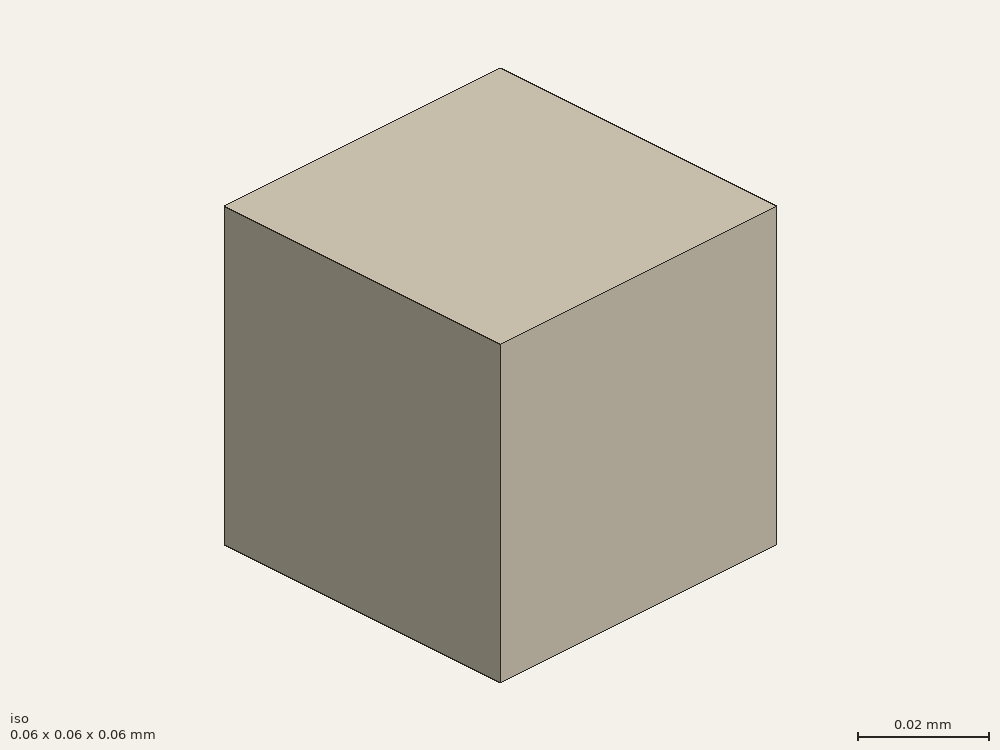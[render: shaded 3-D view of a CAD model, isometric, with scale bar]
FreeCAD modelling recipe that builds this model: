
FCSTD DOCUMENT  (FreeCAD 0.21R33694 (Git))
Label: dipole
License: All rights reserved
LicenseURL: http://en.wikipedia.org/wiki/All_rights_reserved
objects: Part::Part2DObjectPython×22, Part::Extrusion×13, Part::Cut×11, App::FeaturePython×9, Part::FeaturePython×8
note: 54 computed .brp shape members not serialized (recipe doc carries the construction recipe); baked Part::Feature solids carry a one-line shape summary decoded from their .brp

FEATURE [Part::Part2DObjectPython] Polygon  # Draft 2D object (typed FeaturePython)
  Area = 0.0027
  ChamferSize = 0
  DrawMode = 0
  FacesNumber = 12
  FilletRadius = 0
  MakeFace = true
  Placement = pos=(0,0,0.05) rot=(0,0,1;0rad)
  Radius = 0.03
FEATURE [Part::Extrusion] Extrude  label="antenna1"
  Base = -> Polygon
  Dir = (0,0,1)
  DirMode = 2
  FaceMakerClass = Part::FaceMakerBullseye
  LengthFwd = 7.45
  LengthRev = 0
  Solid = false
  Symmetric = false
FEATURE [Part::Part2DObjectPython] Polygon002  # Draft 2D object (typed FeaturePython)
  Area = 0.12
  ChamferSize = 0
  DrawMode = 0
  FacesNumber = 12
  FilletRadius = 0
  MakeFace = true
  Radius = 0.2
FEATURE [Part::Part2DObjectPython] Polygon003  # Draft 2D object (typed FeaturePython)
  Area = 0.48
  ChamferSize = 0
  DrawMode = 0
  FacesNumber = 12
  FilletRadius = 0
  MakeFace = true
  Radius = 0.4
FEATURE [Part::Part2DObjectPython] Polygon004  # Draft 2D object (typed FeaturePython)
  Area = 27
  ChamferSize = 0
  DrawMode = 0
  FacesNumber = 12
  FilletRadius = 0
  MakeFace = true
  Radius = 3
FEATURE [Part::Part2DObjectPython] Polygon005  # Draft 2D object (typed FeaturePython)
  Area = 3
  ChamferSize = 0
  DrawMode = 0
  FacesNumber = 12
  FilletRadius = 0
  MakeFace = true
  Radius = 1
FEATURE [Part::Part2DObjectPython] Polygon006  # Draft 2D object (typed FeaturePython)
  Area = 300
  ChamferSize = 0
  DrawMode = 0
  FacesNumber = 12
  FilletRadius = 0
  MakeFace = true
  Radius = 10
FEATURE [Part::Extrusion] Extrude002
  Base = -> Polygon002
  Dir = (0,0,1)
  DirMode = 2
  FaceMakerClass = Part::FaceMakerBullseye
  LengthFwd = 16
  LengthRev = 0
  Placement = pos=(0,0,-8) rot=(0,0,1;0rad)
  Solid = false
  Symmetric = false
FEATURE [Part::Extrusion] Extrude003
  Base = -> Polygon003
  Dir = (0,0,1)
  DirMode = 2
  FaceMakerClass = Part::FaceMakerBullseye
  LengthFwd = 17
  LengthRev = 0
  Placement = pos=(0,0,-8.5) rot=(0,0,1;0rad)
  Solid = false
  Symmetric = false
FEATURE [Part::Extrusion] Extrude004  label="Extrude005"
  Base = -> Polygon004
  Dir = (0,0,1)
  DirMode = 2
  FaceMakerClass = Part::FaceMakerBullseye
  LengthFwd = 24
  LengthRev = 0
  Placement = pos=(0,0,-12) rot=(0,0,1;0rad)
  Solid = false
  Symmetric = false
FEATURE [Part::Extrusion] Extrude005  label="Extrude004"
  Base = -> Polygon005
  Dir = (0,0,1)
  DirMode = 2
  FaceMakerClass = Part::FaceMakerBullseye
  LengthFwd = 20
  LengthRev = 0
  Placement = pos=(0,0,-10) rot=(0,0,1;0rad)
  Solid = false
  Symmetric = false
FEATURE [Part::Extrusion] Extrude006
  Base = -> Polygon006
  Dir = (0,0,1)
  DirMode = 2
  FaceMakerClass = Part::FaceMakerBullseye
  LengthFwd = 30
  LengthRev = 0
  Placement = pos=(0,0,-15) rot=(0,0,1;0rad)
  Solid = false
  Symmetric = false
FEATURE [Part::Part2DObjectPython] Rectangle  # Draft 2D object (typed FeaturePython)
  Area = 3600
  ChamferSize = 0
  Columns = 1
  FilletRadius = 0
  Height = 60
  Length = 60
  MakeFace = true
  Placement = pos=(-30,-30,0) rot=(0,0,1;0rad)
  Rows = 1
FEATURE [Part::Extrusion] Extrude007  label="air"
  Base = -> Rectangle
  Dir = (0,0,1)
  DirMode = 2
  FaceMakerClass = Part::FaceMakerBullseye
  LengthFwd = 60
  LengthRev = 0
  Placement = pos=(0,0,-30) rot=(0,0,1;0rad)
  Solid = false
  Symmetric = false
FEATURE [App::FeaturePython] Text  label="_Bfront(radiation){front}"  # WARN: FeaturePython — macro-defined, semantics opaque (R4)
  Placement = pos=(-0.0201828,0.0952149,0.04) rot=(0,0,1;0rad)
  Text = .
FEATURE [App::FeaturePython] Text001  label="_Bback(radiation){back}"  # WARN: FeaturePython — macro-defined, semantics opaque (R4)
  Placement = pos=(-0.0201828,0.0952149,0.04) rot=(0,0,1;0rad)
  Text = .
FEATURE [App::FeaturePython] Text002  label="_Bleft(radiation){left}"  # WARN: FeaturePython — macro-defined, semantics opaque (R4)
  Placement = pos=(-0.0201828,0.0952149,0.04) rot=(0,0,1;0rad)
  Text = .
FEATURE [App::FeaturePython] Text003  label="_Bright(radiation){right}"  # WARN: FeaturePython — macro-defined, semantics opaque (R4)
  Placement = pos=(-0.0201828,0.0952149,0.04) rot=(0,0,1;0rad)
  Text = .
FEATURE [App::FeaturePython] Text004  label="_Btop(radiation){top}"  # WARN: FeaturePython — macro-defined, semantics opaque (R4)
  Placement = pos=(-0.0201828,0.0952149,0.04) rot=(0,0,1;0rad)
  Text = .
FEATURE [App::FeaturePython] Text005  label="_Sin(PV){port}"  # WARN: FeaturePython — macro-defined, semantics opaque (R4)
  Placement = pos=(-0.0201828,0.0952149,0.04) rot=(0,0,1;0rad)
  Text = .
FEATURE [App::FeaturePython] Text006  label="_Lin(1,voltage){v}"  # WARN: FeaturePython — macro-defined, semantics opaque (R4)
  Placement = pos=(-0.0201828,0.0952149,0.04) rot=(0,0,1;0rad)
  Text = .
FEATURE [App::FeaturePython] Text007  label="_Lin(1,current){i}"  # WARN: FeaturePython — macro-defined, semantics opaque (R4)
  Placement = pos=(-0.0201828,0.0952149,0.04) rot=(0,0,1;0rad)
  Text = .
FEATURE [Part::Part2DObjectPython] Polygon007  # Draft 2D object (typed FeaturePython)
  Area = 0.0027
  ChamferSize = 0
  DrawMode = 0
  FacesNumber = 12
  FilletRadius = 0
  MakeFace = true
  Placement = pos=(0,0,-0.05) rot=(0,0,1;0rad)
  Radius = 0.03
FEATURE [Part::Extrusion] Extrude008  label="antenna2"
  Base = -> Polygon007
  Dir = (0,0,1)
  DirMode = 2
  FaceMakerClass = Part::FaceMakerBullseye
  LengthFwd = -7.45
  LengthRev = 0
  Solid = false
  Symmetric = false
FEATURE [Part::Part2DObjectPython] Rectangle006  # Draft 2D object (typed FeaturePython)
  Area = 0.0018
  ChamferSize = 0
  Columns = 1
  FilletRadius = 0
  Height = 0.02
  Length = 0.09
  MakeFace = true
  Placement = pos=(-0.045,0,0.03) rot=(1,0,0;1.5708rad)
  Rows = 1
FEATURE [Part::Part2DObjectPython] Rectangle007  # Draft 2D object (typed FeaturePython)
  Area = 0.0018
  ChamferSize = 0
  Columns = 1
  FilletRadius = 0
  Height = 0.02
  Length = 0.09
  MakeFace = true
  Placement = pos=(-0.045,0,-0.05) rot=(1,0,0;1.5708rad)
  Rows = 1
FEATURE [Part::Extrusion] Extrude009  label="plate2"
  Base = -> Rectangle006
  Dir = (0,-1,2e-16)
  DirMode = 2
  FaceMakerClass = Part::FaceMakerBullseye
  LengthFwd = 0.09
  LengthRev = 0
  Placement = pos=(0,0.045,0) rot=(0,0,1;0rad)
  Solid = false
  Symmetric = false
FEATURE [Part::Extrusion] Extrude010  label="plate1"
  Base = -> Rectangle007
  Dir = (0,-1,2e-16)
  DirMode = 2
  FaceMakerClass = Part::FaceMakerBullseye
  LengthFwd = 0.09
  LengthRev = 0
  Placement = pos=(0,0.045,0) rot=(0,0,1;0rad)
  Solid = false
  Symmetric = false
FEATURE [Part::Part2DObjectPython] Rectangle008  # Draft 2D object (typed FeaturePython)
  Area = 0.0225
  ChamferSize = 0
  Columns = 1
  FilletRadius = 0
  Height = 0.15
  Length = 0.15
  MakeFace = true
  Placement = pos=(-0.075,-0.045,-0.075) rot=(1,0,0;1.5708rad)
  Rows = 1
FEATURE [Part::Extrusion] Extrude012  label="void"
  Base = -> Rectangle008
  Dir = (0,-1,2e-16)
  DirMode = 2
  FaceMakerClass = Part::FaceMakerBullseye
  LengthFwd = 0.02
  LengthRev = 0
  Solid = false
  Symmetric = false
FEATURE [Part::Part2DObjectPython] Rectangle010  label="_Pfront"  # Draft 2D object (typed FeaturePython)
  Area = 0.0036
  ChamferSize = 0
  Columns = 1
  FilletRadius = 0
  Height = 0.06
  Length = 0.06
  MakeFace = true
  Placement = pos=(-0.03,-0.03,-0.03) rot=(1,0,0;1.5708rad)
  Rows = 1
FEATURE [Part::Part2DObjectPython] Rectangle011  label="_Pback"  # Draft 2D object (typed FeaturePython)
  Area = 0.0036
  ChamferSize = 0
  Columns = 1
  FilletRadius = 0
  Height = 0.06
  Length = 0.06
  MakeFace = true
  Placement = pos=(-0.03,0.03,-0.03) rot=(1,0,0;1.5708rad)
  Rows = 1
FEATURE [Part::Part2DObjectPython] Rectangle012  label="_Pright"  # Draft 2D object (typed FeaturePython)
  Area = 0.0036
  ChamferSize = 0
  Columns = 1
  FilletRadius = 0
  Height = 0.06
  Length = 0.06
  MakeFace = true
  Placement = pos=(0.03,-0.03,-0.03) rot=(0.57735,0.57735,0.57735;2.0944rad)
  Rows = 1
FEATURE [Part::Part2DObjectPython] Rectangle013  label="_Pleft"  # Draft 2D object (typed FeaturePython)
  Area = 0.0036
  ChamferSize = 0
  Columns = 1
  FilletRadius = 0
  Height = 0.06
  Length = 0.06
  MakeFace = true
  Placement = pos=(-0.03,-0.03,-0.03) rot=(0.57735,0.57735,0.57735;2.0944rad)
  Rows = 1
FEATURE [Part::Part2DObjectPython] Rectangle014  label="_Ptop"  # Draft 2D object (typed FeaturePython)
  Area = 0.0036
  ChamferSize = 0
  Columns = 1
  FilletRadius = 0
  Height = 0.06
  Length = 0.06
  MakeFace = true
  Placement = pos=(-0.03,-0.03,0.03) rot=(0,0,1;0rad)
  Rows = 1
FEATURE [Part::Part2DObjectPython] Rectangle015  label="_Pbottom"  # Draft 2D object (typed FeaturePython)
  Area = 0.0036
  ChamferSize = 0
  Columns = 1
  FilletRadius = 0
  Height = 0.06
  Length = 0.06
  MakeFace = true
  Placement = pos=(-0.03,-0.03,-0.03) rot=(0,0,1;0rad)
  Rows = 1
FEATURE [App::FeaturePython] Text008  label="_Bbottom(radiation){bottom}"  # WARN: FeaturePython — macro-defined, semantics opaque (R4)
  Placement = pos=(-0.0201828,0.0952149,0.04) rot=(0,0,1;0rad)
  Text = .
FEATURE [Part::Part2DObjectPython] Rectangle018  # Draft 2D object (typed FeaturePython)
  Area = 0.0045
  ChamferSize = 0
  Columns = 1
  FilletRadius = 0
  Height = 0.05
  Length = 0.09
  MakeFace = true
  Placement = pos=(-0.045,-0.045,-0.025) rot=(1,0,0;1.5708rad)
  Rows = 1
FEATURE [Part::Extrusion] Extrude013  label="fill"
  Base = -> Rectangle018
  Dir = (0,-1,2e-16)
  DirMode = 2
  FaceMakerClass = Part::FaceMakerBullseye
  LengthFwd = -0.09
  LengthRev = 0
  Solid = false
  Symmetric = false
FEATURE [Part::Part2DObjectPython] Rectangle020  label="_Pi"  # Draft 2D object (typed FeaturePython)
  Area = 2.25e-09
  ChamferSize = 0
  Columns = 1
  FilletRadius = 0
  Height = 2.5e-05
  Length = 9e-05
  MakeFace = true
  Placement = pos=(-4.5e-05,-4.5e-05,-5e-05) rot=(1,0,0;1.5708rad)
  Rows = 1
FEATURE [Part::Part2DObjectPython] Line  label="_Pv"  # Draft 2D object (typed FeaturePython)
  Area = 0
  ChamferSize = 0
  Closed = false
  End = (0,-4.5e-05,2.5e-05)
  FilletRadius = 0
  Length = 6.72681e-05
  MakeFace = true
  Placement = pos=(-4.5e-05,-4.5e-05,-2.5e-05) rot=(1,0,0;1.5708rad)
  Points = (2) [(0,0,0),(4.5e-05,5e-05,3.37458e-18)]
  Start = (-4.5e-05,-4.5e-05,-2.5e-05)
  Subdivisions = 0
FEATURE [Part::Part2DObjectPython] Polygon008  # Draft 2D object (typed FeaturePython)
  Area = 0.0432
  ChamferSize = 0
  DrawMode = 0
  FacesNumber = 12
  FilletRadius = 0
  MakeFace = true
  Radius = 0.12
FEATURE [Part::Extrusion] Extrude014  label="Extrude001"
  Base = -> Polygon008
  Dir = (0,0,1)
  DirMode = 2
  FaceMakerClass = Part::FaceMakerBullseye
  LengthFwd = 15.5
  LengthRev = 0
  Placement = pos=(0,0,-7.75) rot=(0,0,1;0rad)
  Solid = false
  Symmetric = false
FEATURE [Part::Cut] Cut
  Base = -> Extrude007
  Tool = -> Extrude006
FEATURE [Part::FeaturePython] Clone  label="Extrude006clone"  # Draft clone (typed FeaturePython)
  AttacherType = Attacher::AttachEngine3D
  Fuse = false
  Objects = -> [Extrude006]
  Placement = pos=(0,0,-15) rot=(0,0,1;0rad)
  Scale = (1,1,1)
FEATURE [Part::FeaturePython] Clone001  label="Extrude005clone"  # Draft clone (typed FeaturePython)
  AttacherType = Attacher::AttachEngine3D
  Fuse = false
  Objects = -> [Extrude004]
  Placement = pos=(0,0,-12) rot=(0,0,1;0rad)
  Scale = (1,1,1)
FEATURE [Part::FeaturePython] Clone002  label="Extrude004clone"  # Draft clone (typed FeaturePython)
  AttacherType = Attacher::AttachEngine3D
  Fuse = false
  Objects = -> [Extrude005]
  Placement = pos=(0,0,-10) rot=(0,0,1;0rad)
  Scale = (1,1,1)
FEATURE [Part::FeaturePython] Clone003  label="Extrude003clone"  # Draft clone (typed FeaturePython)
  AttacherType = Attacher::AttachEngine3D
  Fuse = false
  Objects = -> [Extrude003]
  Placement = pos=(0,0,-8.5) rot=(0,0,1;0rad)
  Scale = (1,1,1)
FEATURE [Part::FeaturePython] Clone004  label="Extrude002clone"  # Draft clone (typed FeaturePython)
  AttacherType = Attacher::AttachEngine3D
  Fuse = false
  Objects = -> [Extrude002]
  Placement = pos=(0,0,-8) rot=(0,0,1;0rad)
  Scale = (1,1,1)
FEATURE [Part::Cut] Cut001
  Base = -> Clone
  Tool = -> Extrude004
FEATURE [Part::Cut] Cut002
  Base = -> Clone001
  Tool = -> Extrude005
FEATURE [Part::Cut] Cut003
  Base = -> Clone002
  Tool = -> Extrude003
FEATURE [Part::Cut] Cut004
  Base = -> Clone003
  Tool = -> Extrude002
FEATURE [Part::FeaturePython] Clone005  label="Extrude001clone"  # Draft clone (typed FeaturePython)
  AttacherType = Attacher::AttachEngine3D
  Fuse = false
  Objects = -> [Extrude014]
  Placement = pos=(0,0,-7.75) rot=(0,0,1;0rad)
  Scale = (1,1,1)
FEATURE [Part::Cut] Cut005
  Base = -> Clone004
  Tool = -> Extrude014
FEATURE [Part::Cut] Cut006
  Base = -> Clone005
  Tool = -> Extrude
FEATURE [Part::Cut] Cut007
  Base = -> Cut006
  Tool = -> Extrude008
FEATURE [Part::Cut] Cut008
  Base = -> Cut007
  Tool = -> Extrude010
FEATURE [Part::Cut] Cut009
  Base = -> Cut008
  Tool = -> Extrude009
FEATURE [Part::Cut] Cut010
  Base = -> Cut009
  Tool = -> Extrude012
FEATURE [Part::Part2DObjectPython] Rectangle021  label="_Pport"  # Draft 2D object (typed FeaturePython)
  Area = 2.25e-08
  ChamferSize = 0
  Columns = 1
  FilletRadius = 0
  Height = 0.00015
  Length = 0.00015
  MakeFace = true
  Placement = pos=(-7.5e-05,-4.5e-05,-7.5e-05) rot=(1,0,0;1.5708rad)
  Rows = 1
FEATURE [Part::FeaturePython] BooleanFragments  # WARN: FeaturePython — macro-defined, semantics opaque (R4)
  Mode = 0
  Objects = -> [Extrude013,Cut,Cut001,Cut002,Cut003,Cut004,Cut005,Cut010]
  Tolerance = 0
FEATURE [Part::FeaturePython] Clone006  label="scaled"  # Draft clone (typed FeaturePython)
  AttacherType = Attacher::AttachEngine3D
  Fuse = false
  Objects = -> [BooleanFragments]
  Scale = (0.001,0.001,0.001)
